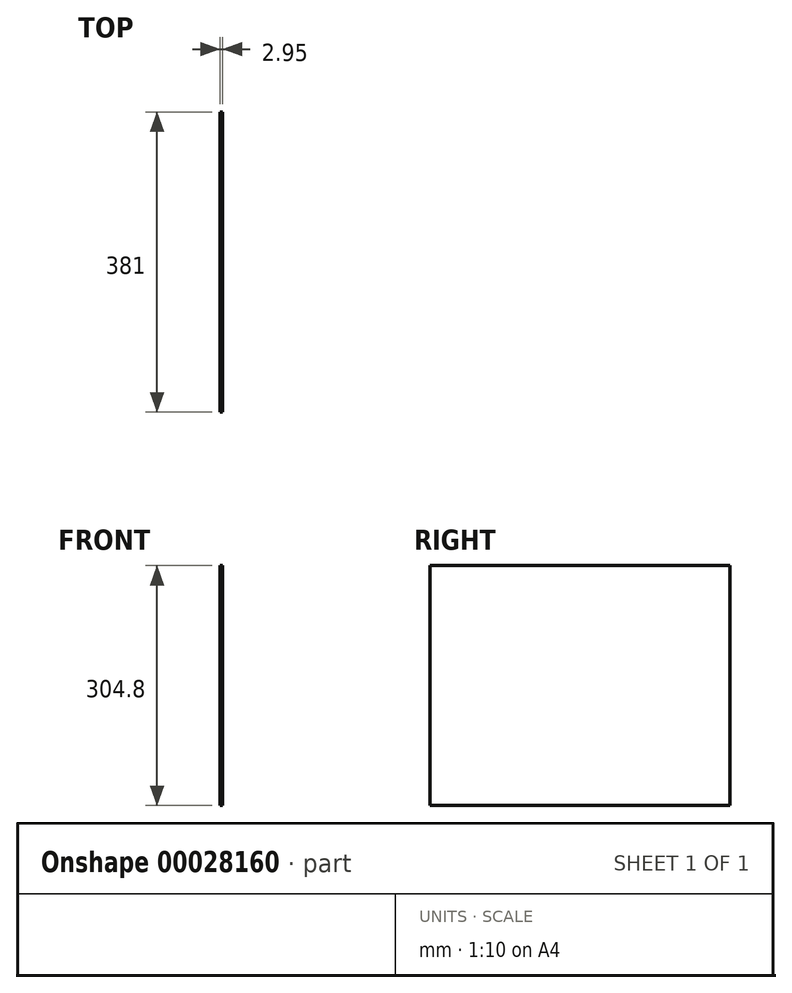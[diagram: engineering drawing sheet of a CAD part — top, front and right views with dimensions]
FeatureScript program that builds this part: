
annotation { "Feature Type Name" : "Feature", "Feature Type Description" : "" }
export const myFeature = defineFeature(function(context is Context, id is Id, definition is map)
    precondition{}
    {
        {
            var Q0;
            Q0=qCreatedBy(makeId("Right.planeOp"),FACE);
            var sketch = newSketch(context, id + "F0", { "sketchPlane" : qUnion([Q0])});
            skLineSegment(sketch, "E0.bottom", {"start": v(0, 0) * mm, "end": v(381, 0) * mm});
            skLineSegment(sketch, "E0.top", {"start": v(0, 304.8) * mm, "end": v(381, 304.8) * mm});
            skLineSegment(sketch, "E0.left", {"start": v(0, 0) * mm, "end": v(0, 304.8) * mm});
            skLineSegment(sketch, "E0.right", {"start": v(381, 0) * mm, "end": v(381, 304.8) * mm});
            skSolve(sketch);
        }
        {
            var Q0;
            Q0 = qSketchRegion(id + "F0", true);
            extrude(context, id + "F1", {"entities" : qUnion([Q0]), "depth" : 2.95 * mm});
        }
    });
